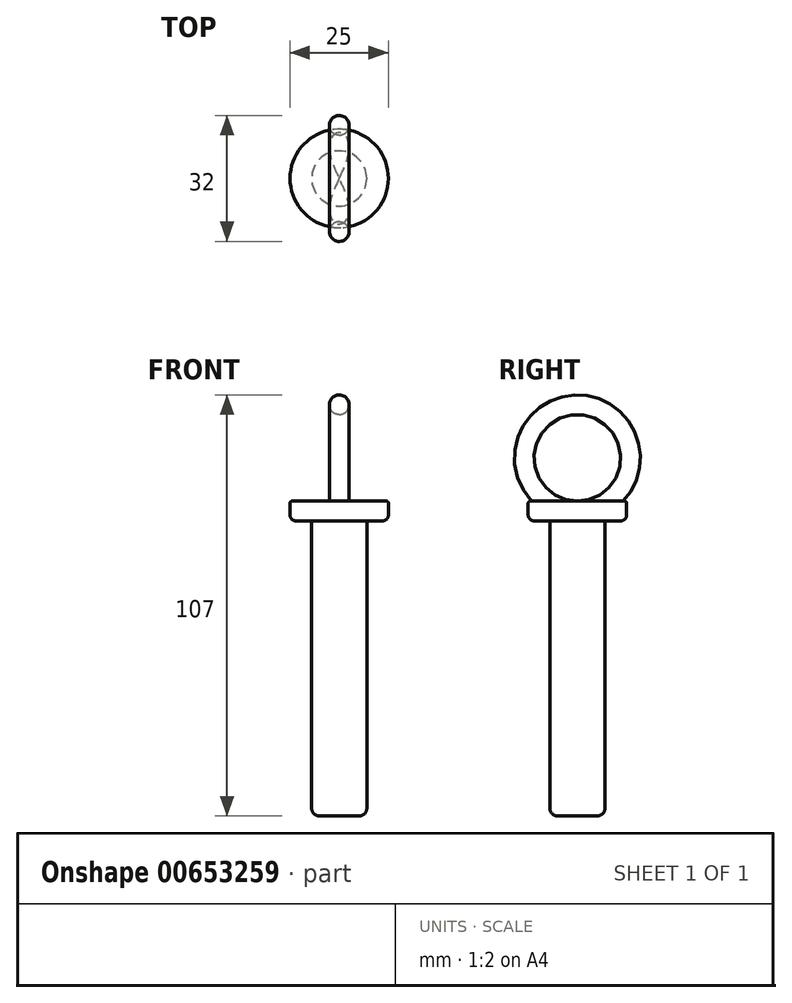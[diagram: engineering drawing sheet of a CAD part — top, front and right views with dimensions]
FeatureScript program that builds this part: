
annotation { "Feature Type Name" : "Feature", "Feature Type Description" : "" }
export const myFeature = defineFeature(function(context is Context, id is Id, definition is map)
    precondition{}
    {
        {
            var Q0;
            Q0=qCreatedBy(makeId("Top.planeOp"),FACE);
            var sketch = newSketch(context, id + "F0", { "sketchPlane" : qUnion([Q0])});
            skCircle(sketch, "E0", {"center": v(0, 0) * mm, "radius": 7 * mm});
            skSolve(sketch);
        }
        {
            var Q0;
            Q0 = qSketchRegion(id + "F0", true);
            extrude(context, id + "F1", {"entities" : qUnion([Q0]), "flatOperationType" : FlatOperationType.REMOVE, "depth" : 75 * mm, "offsetDistance" : 25 * mm, "domain" : OperationDomain.MODEL});
        }
        {
            var Q0;
            Q0=makeQuery(id+"F1.opExtrude","CAP_FACE",FACE,{"disambiguationData":[OSD([sQuery(id+"F0.wireOp",EDGE,"E0")])],"isStart":false});
            var sketch = newSketch(context, id + "F2", { "sketchPlane" : qUnion([Q0])});
            skCircle(sketch, "E1", {"center": v(0, 0) * mm, "radius": 12.5 * mm});
            skSolve(sketch);
        }
        {
            var Q0;
            Q0 = qSketchRegion(id + "F2", true);
            extrude(context, id + "F3", {"entities" : qUnion([Q0]), "operationType" : NewBodyOperationType.ADD, "depth" : 5 * mm, "offsetDistance" : 25 * mm});
        }
        {
            var Q0;
            Q0=qCreatedBy(makeId("Right.planeOp"),FACE);
            var sketch = newSketch(context, id + "F4", { "sketchPlane" : qUnion([Q0])});
            skCircle(sketch, "E2", {"center": v(0, 91) * mm, "radius": 12.5 * mm});
            skSolve(sketch);
        }
        {
            var Q0;
            Q0=qCreatedBy(makeId("Front.planeOp"),FACE);
            var sketch = newSketch(context, id + "F5", { "sketchPlane" : qUnion([Q0])});
            skCircle(sketch, "E3", {"center": v(0, 77.5) * mm, "radius": 2.5 * mm});
            skSolve(sketch);
        }
        {
            var Q0;
            Q0 = qSketchRegion(id + "F5", true);
            var Q1;
            Q1 = qConstructionFilter(qBodyType(qCreatedBy(id + "F4" ,EDGE), BodyType.WIRE), ConstructionObject.NO);
            sweep(context, id + "F6", {"operationType" : NewBodyOperationType.ADD, "profiles" : qUnion([Q0]), "path" : qUnion([Q1])});
        }
        {
            var Q0;
            Q0=makeQuery(id+"F1.opExtrude","CAP_EDGE",EDGE,{"disambiguationData":[OSD([sQuery(id+"F0.wireOp",EDGE,"E0")])],"isStart":false});
            var Q1;
            Q1=makeQuery(id+"F3.opExtrude","CAP_EDGE",EDGE,{"disambiguationData":[OSD([sQuery(id+"F2.wireOp",EDGE,"E1")])],"isStart":true});
            fillet(context, id + "F7", {"entities" : qUnion([Q0, Q1]), "radius" : 1.5 * mm, "tangentPropagation" : true, "allowEdgeOverflow" : false});
        }
        {
            var Q0;
            Q0=makeQuery(id+"F3.opExtrude","CAP_EDGE",EDGE,{"disambiguationData":[OSD([sQuery(id+"F2.wireOp",EDGE,"E1")])],"isStart":false});
            fillet(context, id + "F8", {"entities" : qUnion([Q0]), "radius" : .5 * mm, "tangentPropagation" : true, "allowEdgeOverflow" : false});
        }
        {
            var Q0;
            Q0=makeQuery(id+"F1.opExtrude","CAP_EDGE",EDGE,{"disambiguationData":[OSD([sQuery(id+"F0.wireOp",EDGE,"E0")])],"isStart":true});
            fillet(context, id + "F9", {"entities" : qUnion([Q0]), "radius" : 2 * mm, "tangentPropagation" : true, "allowEdgeOverflow" : false});
        }
    });
